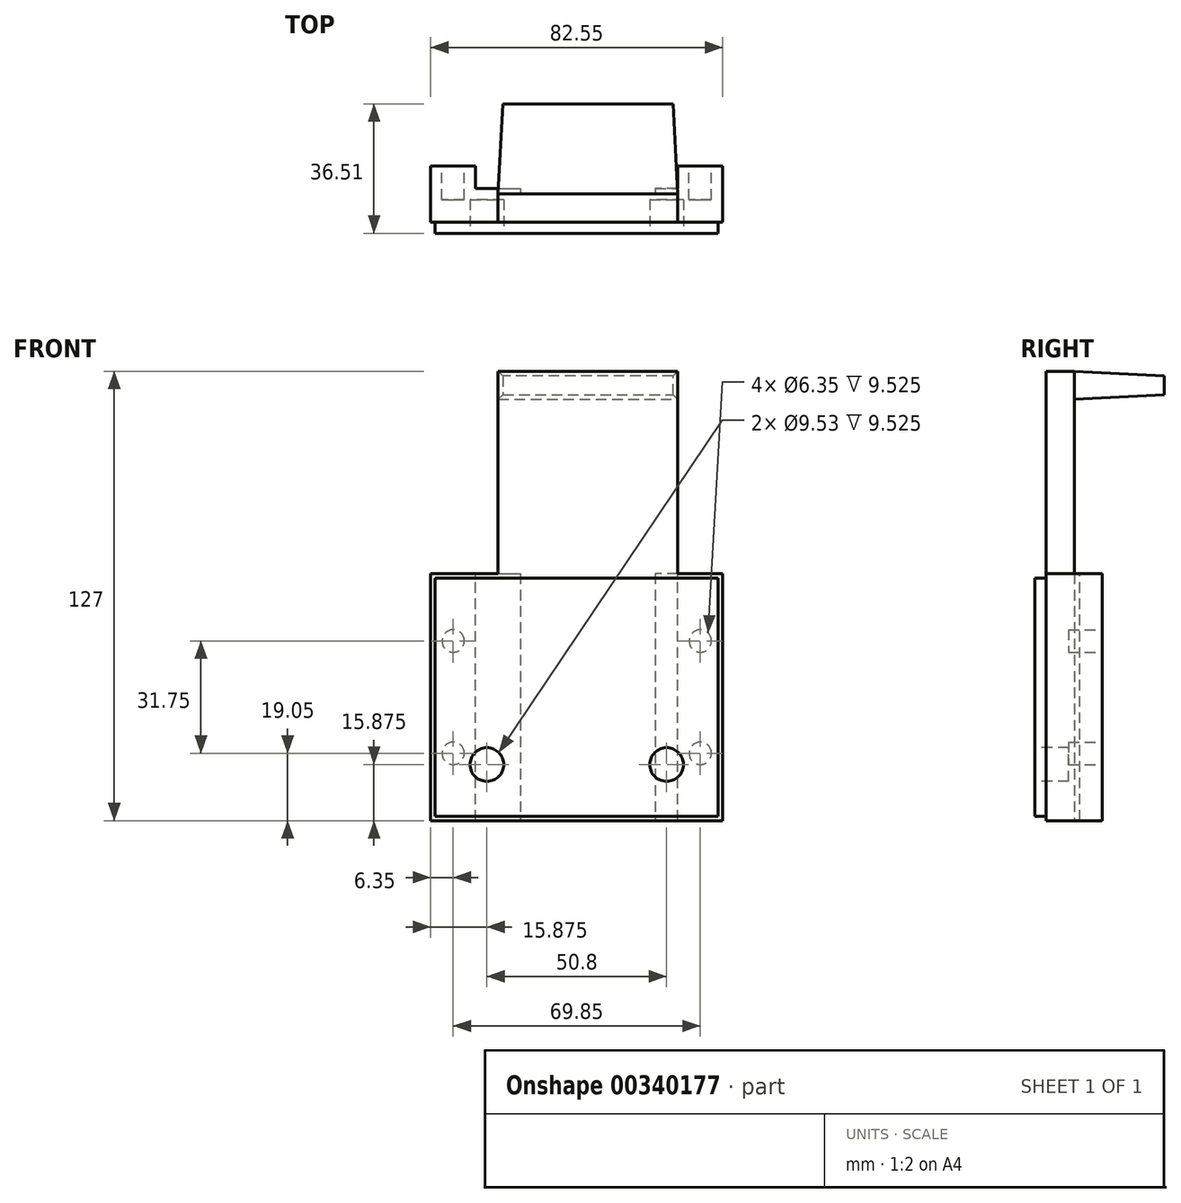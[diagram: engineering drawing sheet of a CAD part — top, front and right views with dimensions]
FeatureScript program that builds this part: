
annotation { "Feature Type Name" : "Feature", "Feature Type Description" : "" }
export const myFeature = defineFeature(function(context is Context, id is Id, definition is map)
    precondition{}
    {
        {
            var Q0;
            Q0=qCreatedBy(makeId("Front.planeOp"),FACE);
            var sketch = newSketch(context, id + "F0", { "sketchPlane" : qUnion([Q0])});
            skLineSegment(sketch, "E0.bottom", {"start": v(0, 0) * mm, "end": v(82.55, 0) * mm});
            skLineSegment(sketch, "E0.top", {"start": v(0, 69.85) * mm, "end": v(82.55, 69.85) * mm});
            skLineSegment(sketch, "E0.left", {"start": v(0, 0) * mm, "end": v(0, 69.85) * mm});
            skLineSegment(sketch, "E0.right", {"start": v(82.55, 0) * mm, "end": v(82.55, 69.85) * mm});
            skLineSegment(sketch, "E1.bottom", {"start": v(19.05, 69.85) * mm, "end": v(69.85, 69.85) * mm});
            skLineSegment(sketch, "E1.top", {"start": v(19.05, 127) * mm, "end": v(69.85, 127) * mm});
            skLineSegment(sketch, "E1.left", {"start": v(19.05, 69.85) * mm, "end": v(19.05, 127) * mm});
            skLineSegment(sketch, "E1.right", {"start": v(69.85, 69.85) * mm, "end": v(69.85, 127) * mm});
            skSolve(sketch);
        }
        {
            var Q0;
            Q0 = qSketchRegion(id + "F0", true);
            extrude(context, id + "F1", {"entities" : qUnion([Q0]), "depth" : 7.94 * mm});
        }
        {
            var Q0;
            Q0=makeQuery(id+"F1.opExtrude","CAP_FACE",FACE,{"disambiguationData":[OSD([sQuery(id+"F0.wireOp",EDGE,"E0.bottom"),sQuery(id+"F0.wireOp",EDGE,"E0.top"),sQuery(id+"F0.wireOp",EDGE,"E0.left"),sQuery(id+"F0.wireOp",EDGE,"E0.right"),sQuery(id+"F0.wireOp",EDGE,"E1.top"),sQuery(id+"F0.wireOp",EDGE,"E1.left"),sQuery(id+"F0.wireOp",EDGE,"E1.right")])],"isStart":true});
            var sketch = newSketch(context, id + "F2", { "sketchPlane" : qUnion([Q0])});
            skLineSegment(sketch, "E2.bottom", {"start": v(0, 0) * mm, "end": v(-12.7, 0) * mm});
            skLineSegment(sketch, "E2.top", {"start": v(0, 69.85) * mm, "end": v(-12.7, 69.85) * mm});
            skLineSegment(sketch, "E2.left", {"start": v(0, 0) * mm, "end": v(0, 69.85) * mm});
            skLineSegment(sketch, "E2.right", {"start": v(-12.7, 0) * mm, "end": v(-12.7, 69.85) * mm});
            skLineSegment(sketch, "E3.bottom", {"start": v(-82.55, 0) * mm, "end": v(-69.85, 0) * mm});
            skLineSegment(sketch, "E3.top", {"start": v(-82.55, 69.85) * mm, "end": v(-69.85, 69.85) * mm});
            skLineSegment(sketch, "E3.left", {"start": v(-82.55, 0) * mm, "end": v(-82.55, 69.85) * mm});
            skLineSegment(sketch, "E3.right", {"start": v(-69.85, 0) * mm, "end": v(-69.85, 69.85) * mm});
            skSolve(sketch);
        }
        {
            var Q0;
            Q0 = qSketchRegion(id + "F2", true);
            extrude(context, id + "F3", {"entities" : qUnion([Q0]), "operationType" : NewBodyOperationType.ADD, "depth" : 7.94 * mm});
        }
        {
            var Q0;
            Q0=makeQuery(id+"F1.opExtrude","CAP_FACE",FACE,{"disambiguationData":[OSD([sQuery(id+"F0.wireOp",EDGE,"E0.bottom"),sQuery(id+"F0.wireOp",EDGE,"E0.top"),sQuery(id+"F0.wireOp",EDGE,"E0.left"),sQuery(id+"F0.wireOp",EDGE,"E0.right"),sQuery(id+"F0.wireOp",EDGE,"E1.top"),sQuery(id+"F0.wireOp",EDGE,"E1.left"),sQuery(id+"F0.wireOp",EDGE,"E1.right")])],"isStart":true});
            var sketch = newSketch(context, id + "F4", { "sketchPlane" : qUnion([Q0])});
            skLineSegment(sketch, "E4.bottom", {"start": v(-12.7, 69.85) * mm, "end": v(-25.4, 69.85) * mm});
            skLineSegment(sketch, "E4.top", {"start": v(-12.7, 0) * mm, "end": v(-25.4, 0) * mm});
            skLineSegment(sketch, "E4.left", {"start": v(-12.7, 69.85) * mm, "end": v(-12.7, 0) * mm});
            skLineSegment(sketch, "E4.right", {"start": v(-25.4, 69.85) * mm, "end": v(-25.4, 0) * mm});
            skLineSegment(sketch, "E5.bottom", {"start": v(-69.85, 69.85) * mm, "end": v(-63.5, 69.85) * mm});
            skLineSegment(sketch, "E5.top", {"start": v(-69.85, 0) * mm, "end": v(-63.5, 0) * mm});
            skLineSegment(sketch, "E5.left", {"start": v(-69.85, 69.85) * mm, "end": v(-69.85, 0) * mm});
            skLineSegment(sketch, "E5.right", {"start": v(-63.5, 69.85) * mm, "end": v(-63.5, 0) * mm});
            skSolve(sketch);
        }
        {
            var Q0;
            Q0 = qSketchRegion(id + "F4", true);
            extrude(context, id + "F5", {"entities" : qUnion([Q0]), "operationType" : NewBodyOperationType.ADD, "depth" : 1.59 * mm});
        }
        {
            var Q0;
            Q0=makeQuery(id+"F1.opExtrude","CAP_FACE",FACE,{"disambiguationData":[OSD([sQuery(id+"F0.wireOp",EDGE,"E0.bottom"),sQuery(id+"F0.wireOp",EDGE,"E0.top"),sQuery(id+"F0.wireOp",EDGE,"E0.left"),sQuery(id+"F0.wireOp",EDGE,"E0.right"),sQuery(id+"F0.wireOp",EDGE,"E1.top"),sQuery(id+"F0.wireOp",EDGE,"E1.left"),sQuery(id+"F0.wireOp",EDGE,"E1.right")])],"isStart":true});
            var sketch = newSketch(context, id + "F6", { "sketchPlane" : qUnion([Q0])});
            skLineSegment(sketch, "E6.bottom", {"start": v(-69.85, 127) * mm, "end": v(-19.05, 127) * mm});
            skLineSegment(sketch, "E6.top", {"start": v(-69.85, 119.06) * mm, "end": v(-19.05, 119.06) * mm});
            skLineSegment(sketch, "E6.left", {"start": v(-69.85, 127) * mm, "end": v(-69.85, 119.06) * mm});
            skLineSegment(sketch, "E6.right", {"start": v(-19.05, 127) * mm, "end": v(-19.05, 119.06) * mm});
            skSolve(sketch);
        }
        {
            var Q0;
            Q0 = qSketchRegion(id + "F6", true);
            extrude(context, id + "F7", {"entities" : qUnion([Q0]), "operationType" : NewBodyOperationType.ADD, "depth" : 25.4 * mm, "hasDraft" : true, "draftAngle" : 3 * degree, "draftPullDirection" : true});
        }
        {
            var Q0;
            Q0=makeQuery(id+"F1.opExtrude","CAP_FACE",FACE,{"disambiguationData":[OSD([sQuery(id+"F0.wireOp",EDGE,"E0.bottom"),sQuery(id+"F0.wireOp",EDGE,"E0.top"),sQuery(id+"F0.wireOp",EDGE,"E0.left"),sQuery(id+"F0.wireOp",EDGE,"E0.right"),sQuery(id+"F0.wireOp",EDGE,"E1.top"),sQuery(id+"F0.wireOp",EDGE,"E1.left"),sQuery(id+"F0.wireOp",EDGE,"E1.right")])],"isStart":false});
            var sketch = newSketch(context, id + "F8", { "sketchPlane" : qUnion([Q0])});
            skLineSegment(sketch, "E7.bottom", {"start": v(0, 69.85) * mm, "end": v(82.55, 69.85) * mm});
            skLineSegment(sketch, "E7.top", {"start": v(0, 0) * mm, "end": v(82.55, 0) * mm});
            skLineSegment(sketch, "E7.left", {"start": v(0, 69.85) * mm, "end": v(0, 0) * mm});
            skLineSegment(sketch, "E7.right", {"start": v(82.55, 69.85) * mm, "end": v(82.55, 0) * mm});
            skLineSegment(sketch, "E8.0", {"start": v(1.27, 68.58) * mm, "end": v(1.27, 1.27) * mm});
            skLineSegment(sketch, "E8.1", {"start": v(1.27, 68.58) * mm, "end": v(81.28, 68.58) * mm});
            skLineSegment(sketch, "E8.2", {"start": v(81.28, 68.58) * mm, "end": v(81.28, 1.27) * mm});
            skLineSegment(sketch, "E8.3", {"start": v(1.27, 1.27) * mm, "end": v(81.28, 1.27) * mm});
            skSolve(sketch);
        }
        {
            var Q0;
            Q0=makeQuery(id+"F8.imprint","IMPRINT",FACE,{"disambiguationData":[TD([[makeQuery(id+"F8.imprint","IMPRINT",EDGE,{"derivedFrom":sQuery(id+"F8.wireOp",EDGE,"E8.0")}),1.0]])]});
            extrude(context, id + "F9", {"entities" : qUnion([Q0]), "operationType" : NewBodyOperationType.ADD, "depth" : 3.17 * mm});
        }
        {
            var Q0;
            Q0=makeQuery(id+"F9.opExtrude","CAP_FACE",FACE,{"disambiguationData":[OSD([sQuery(id+"F8.wireOp",EDGE,"E8.0"),sQuery(id+"F8.wireOp",EDGE,"E8.1"),sQuery(id+"F8.wireOp",EDGE,"E8.2"),sQuery(id+"F8.wireOp",EDGE,"E8.3")])],"isStart":false});
            var sketch = newSketch(context, id + "F10", { "sketchPlane" : qUnion([Q0])});
            skCircle(sketch, "E9", {"center": v(15.88, 15.88) * mm, "radius": 4.76 * mm});
            skCircle(sketch, "E10", {"center": v(66.68, 15.88) * mm, "radius": 4.76 * mm});
            skSolve(sketch);
        }
        {
            var Q0;
            Q0 = qSketchRegion(id + "F10", true);
            extrude(context, id + "F11", {"entities" : qUnion([Q0]), "operationType" : NewBodyOperationType.REMOVE, "oppositeDirection" : true, "depth" : 9.52 * mm});
        }
        {
            var Q0;
            Q0=makeQuery(id+"F3.opExtrude","CAP_FACE",FACE,{"disambiguationData":[OSD([sQuery(id+"F2.wireOp",EDGE,"E3.bottom"),sQuery(id+"F2.wireOp",EDGE,"E3.top"),sQuery(id+"F2.wireOp",EDGE,"E3.left"),sQuery(id+"F2.wireOp",EDGE,"E3.right")])],"isStart":false});
            var sketch = newSketch(context, id + "F12", { "sketchPlane" : qUnion([Q0])});
            skCircle(sketch, "E11", {"center": v(-76.2, 50.8) * mm, "radius": 3.18 * mm});
            skCircle(sketch, "E12", {"center": v(-76.2, 19.05) * mm, "radius": 3.18 * mm});
            skCircle(sketch, "E13", {"center": v(-6.35, 50.8) * mm, "radius": 3.18 * mm});
            skCircle(sketch, "E14", {"center": v(-6.35, 19.05) * mm, "radius": 3.18 * mm});
            skSolve(sketch);
        }
        {
            var Q0;
            Q0 = qSketchRegion(id + "F12", true);
            extrude(context, id + "F13", {"entities" : qUnion([Q0]), "operationType" : NewBodyOperationType.REMOVE, "oppositeDirection" : true, "depth" : 9.52 * mm});
        }
    });
